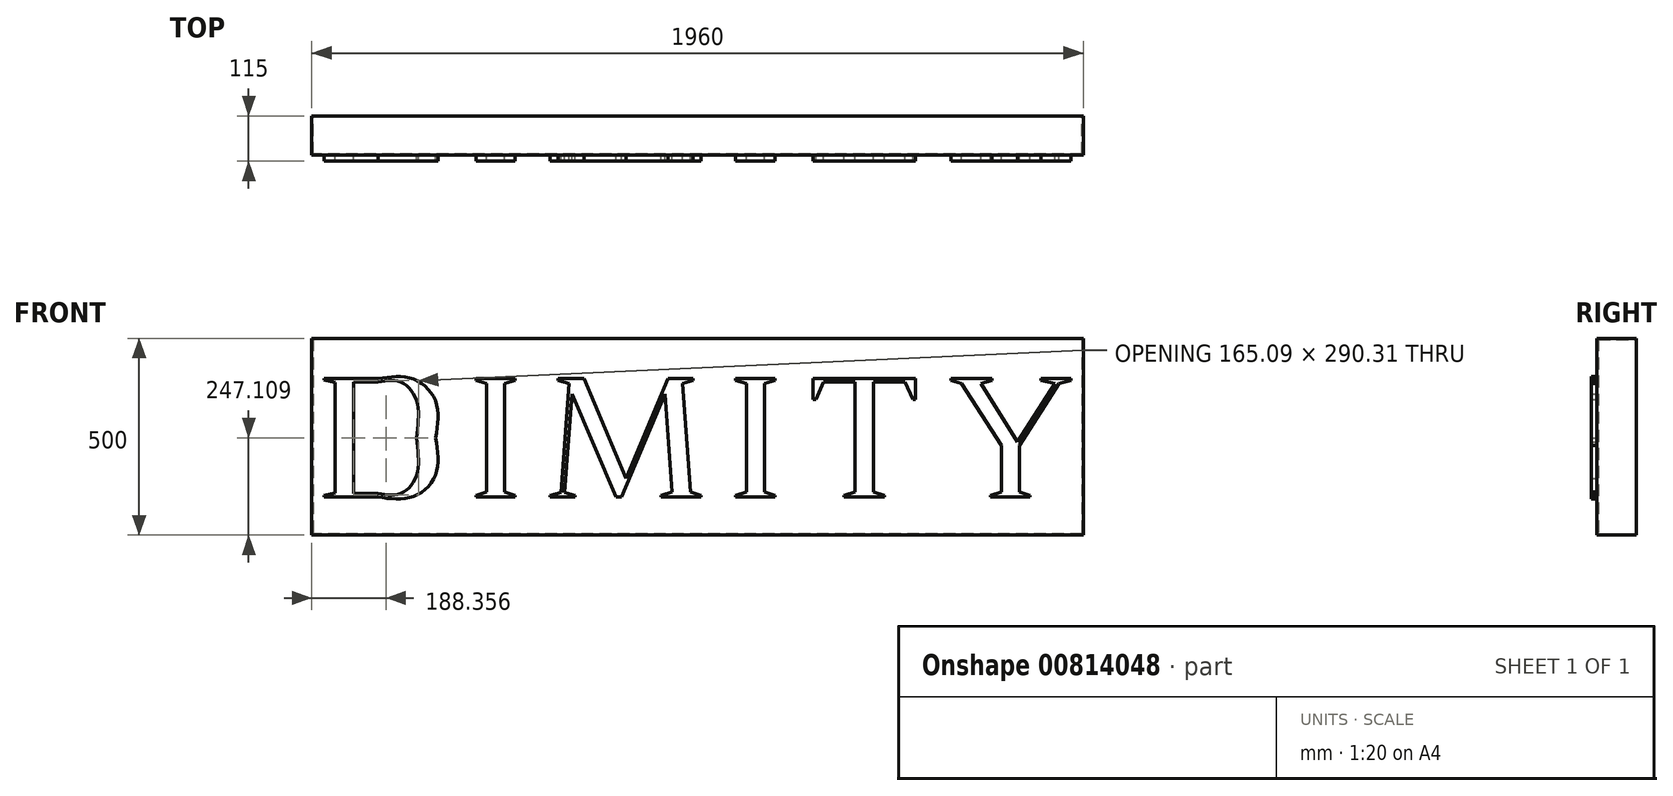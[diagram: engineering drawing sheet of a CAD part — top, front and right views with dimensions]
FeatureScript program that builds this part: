
annotation { "Feature Type Name" : "Feature", "Feature Type Description" : "" }
export const myFeature = defineFeature(function(context is Context, id is Id, definition is map)
    precondition{}
    {
        {
            var Q0;
            Q0=qCreatedBy(makeId("Front.planeOp"),FACE);
            var sketch = newSketch(context, id + "F0", { "sketchPlane" : qUnion([Q0])});
            skLineSegment(sketch, "E0", {"start": v(-948.48, 190.9) * mm, "end": v(-948.48, 187.03) * mm});
            skLineSegment(sketch, "E1", {"start": v(-948.48, 187.03) * mm, "end": v(-920.57, 180.59) * mm});
            skLineSegment(sketch, "E2", {"start": v(-920.57, 180.59) * mm, "end": v(-920.57, -99.41) * mm});
            skLineSegment(sketch, "E3", {"start": v(-920.57, -99.41) * mm, "end": v(-948.48, -106.29) * mm});
            skLineSegment(sketch, "E4", {"start": v(-948.48, -106.29) * mm, "end": v(-948.48, -109.72) * mm});
            skLineSegment(sketch, "E5", {"start": v(-948.48, -109.72) * mm, "end": v(-811.49, -109.72) * mm});
            skFitSpline(sketch, "E6", {"points": [v(-811.49, -109.72) * mm, v(-725.6, -109.72) * mm, v(-665.47, -53.9) * mm, v(-665.47, 40.59) * mm]});
            skFitSpline(sketch, "E7", {"points": [v(-665.47, 40.59) * mm, v(-665.47, 134.2) * mm, v(-725.6, 190.9) * mm, v(-811.49, 190.9) * mm]});
            skLineSegment(sketch, "E8", {"start": v(-811.49, 190.9) * mm, "end": v(-948.48, 190.9) * mm});
            skLineSegment(sketch, "E9", {"start": v(-874.19, 182.3) * mm, "end": v(-811.49, 182.3) * mm});
            skFitSpline(sketch, "E10", {"points": [v(-811.49, 182.3) * mm, v(-754.8, 182.3) * mm, v(-714, 135.07) * mm, v(-714, 40.16) * mm]});
            skFitSpline(sketch, "E11", {"points": [v(-714, 40.16) * mm, v(-714, -54.32) * mm, v(-754.8, -101.13) * mm, v(-811.49, -101.13) * mm]});
            skLineSegment(sketch, "E12", {"start": v(-811.49, -101.13) * mm, "end": v(-874.19, -101.13) * mm});
            skLineSegment(sketch, "E13", {"start": v(-874.19, -101.13) * mm, "end": v(-874.19, 182.3) * mm});
            skLineSegment(sketch, "E14", {"start": v(-563.25, 190.9) * mm, "end": v(-563.25, 186.6) * mm});
            skLineSegment(sketch, "E15", {"start": v(-563.25, 186.6) * mm, "end": v(-535.32, 178.44) * mm});
            skLineSegment(sketch, "E16", {"start": v(-535.32, 178.44) * mm, "end": v(-535.32, -97.27) * mm});
            skLineSegment(sketch, "E17", {"start": v(-535.32, -97.27) * mm, "end": v(-563.25, -105.43) * mm});
            skLineSegment(sketch, "E18", {"start": v(-563.25, -105.43) * mm, "end": v(-563.25, -109.72) * mm});
            skLineSegment(sketch, "E19", {"start": v(-563.25, -109.72) * mm, "end": v(-463.18, -109.72) * mm});
            skLineSegment(sketch, "E20", {"start": v(-463.18, -109.72) * mm, "end": v(-463.18, -105.43) * mm});
            skLineSegment(sketch, "E21", {"start": v(-463.18, -105.43) * mm, "end": v(-489.8, -97.27) * mm});
            skLineSegment(sketch, "E22", {"start": v(-489.8, -97.27) * mm, "end": v(-489.8, 178.44) * mm});
            skLineSegment(sketch, "E23", {"start": v(-489.8, 178.44) * mm, "end": v(-463.18, 186.6) * mm});
            skLineSegment(sketch, "E24", {"start": v(-463.18, 186.6) * mm, "end": v(-463.18, 190.9) * mm});
            skLineSegment(sketch, "E25", {"start": v(-463.18, 190.9) * mm, "end": v(-563.25, 190.9) * mm});
            skLineSegment(sketch, "E26", {"start": v(-354.1, 190.9) * mm, "end": v(-354.1, 186.6) * mm});
            skLineSegment(sketch, "E27", {"start": v(-354.1, 186.6) * mm, "end": v(-326.18, 178.44) * mm});
            skLineSegment(sketch, "E28", {"start": v(-326.18, 178.44) * mm, "end": v(-346.37, -98.13) * mm});
            skLineSegment(sketch, "E29", {"start": v(-346.37, -98.13) * mm, "end": v(-374.28, -106.29) * mm});
            skLineSegment(sketch, "E30", {"start": v(-374.28, -106.29) * mm, "end": v(-374.28, -109.72) * mm});
            skLineSegment(sketch, "E31", {"start": v(-374.28, -109.72) * mm, "end": v(-311.15, -109.72) * mm});
            skLineSegment(sketch, "E32", {"start": v(-311.15, -109.72) * mm, "end": v(-311.15, -106.29) * mm});
            skLineSegment(sketch, "E33", {"start": v(-311.15, -106.29) * mm, "end": v(-337.35, -98.13) * mm});
            skLineSegment(sketch, "E34", {"start": v(-337.35, -98.13) * mm, "end": v(-318.88, 151.82) * mm});
            skLineSegment(sketch, "E35", {"start": v(-318.88, 151.82) * mm, "end": v(-206.8, -109.72) * mm});
            skLineSegment(sketch, "E36", {"start": v(-206.8, -109.72) * mm, "end": v(-192.62, -109.72) * mm});
            skLineSegment(sketch, "E37", {"start": v(-192.62, -109.72) * mm, "end": v(-82.25, 151.39) * mm});
            skLineSegment(sketch, "E38", {"start": v(-82.25, 151.39) * mm, "end": v(-64.21, -97.27) * mm});
            skLineSegment(sketch, "E39", {"start": v(-64.21, -97.27) * mm, "end": v(-92.13, -105.43) * mm});
            skLineSegment(sketch, "E40", {"start": v(-92.13, -105.43) * mm, "end": v(-92.13, -109.72) * mm});
            skLineSegment(sketch, "E41", {"start": v(-92.13, -109.72) * mm, "end": v(8.36, -109.72) * mm});
            skLineSegment(sketch, "E42", {"start": v(8.36, -109.72) * mm, "end": v(8.36, -105.43) * mm});
            skLineSegment(sketch, "E43", {"start": v(8.36, -105.43) * mm, "end": v(-18.27, -97.27) * mm});
            skLineSegment(sketch, "E44", {"start": v(-18.27, -97.27) * mm, "end": v(-38.02, 178.44) * mm});
            skLineSegment(sketch, "E45", {"start": v(-38.02, 178.44) * mm, "end": v(-11.4, 186.6) * mm});
            skLineSegment(sketch, "E46", {"start": v(-11.4, 186.6) * mm, "end": v(-11.4, 190.9) * mm});
            skLineSegment(sketch, "E47", {"start": v(-11.4, 190.9) * mm, "end": v(-74.52, 190.9) * mm});
            skLineSegment(sketch, "E48", {"start": v(-74.52, 190.9) * mm, "end": v(-181.03, -62.48) * mm});
            skLineSegment(sketch, "E49", {"start": v(-181.03, -62.48) * mm, "end": v(-288.39, 190.9) * mm});
            skLineSegment(sketch, "E50", {"start": v(-288.39, 190.9) * mm, "end": v(-354.1, 190.9) * mm});
            skLineSegment(sketch, "E51", {"start": v(96.42, 190.9) * mm, "end": v(96.42, 186.6) * mm});
            skLineSegment(sketch, "E52", {"start": v(96.42, 186.6) * mm, "end": v(124.34, 178.44) * mm});
            skLineSegment(sketch, "E53", {"start": v(124.34, 178.44) * mm, "end": v(124.34, -97.27) * mm});
            skLineSegment(sketch, "E54", {"start": v(124.34, -97.27) * mm, "end": v(96.42, -105.43) * mm});
            skLineSegment(sketch, "E55", {"start": v(96.42, -105.43) * mm, "end": v(96.42, -109.72) * mm});
            skLineSegment(sketch, "E56", {"start": v(96.42, -109.72) * mm, "end": v(196.48, -109.72) * mm});
            skLineSegment(sketch, "E57", {"start": v(196.48, -109.72) * mm, "end": v(196.48, -105.43) * mm});
            skLineSegment(sketch, "E58", {"start": v(196.48, -105.43) * mm, "end": v(169.86, -97.27) * mm});
            skLineSegment(sketch, "E59", {"start": v(169.86, -97.27) * mm, "end": v(169.86, 178.44) * mm});
            skLineSegment(sketch, "E60", {"start": v(169.86, 178.44) * mm, "end": v(196.48, 186.6) * mm});
            skLineSegment(sketch, "E61", {"start": v(196.48, 186.6) * mm, "end": v(196.48, 190.9) * mm});
            skLineSegment(sketch, "E62", {"start": v(196.48, 190.9) * mm, "end": v(96.42, 190.9) * mm});
            skLineSegment(sketch, "E63", {"start": v(293.55, 190.9) * mm, "end": v(293.55, 138.07) * mm});
            skLineSegment(sketch, "E64", {"start": v(293.55, 138.07) * mm, "end": v(300.42, 138.07) * mm});
            skLineSegment(sketch, "E65", {"start": v(300.42, 138.07) * mm, "end": v(320.6, 182.3) * mm});
            skLineSegment(sketch, "E66", {"start": v(320.6, 182.3) * mm, "end": v(400.48, 182.3) * mm});
            skLineSegment(sketch, "E67", {"start": v(400.48, 182.3) * mm, "end": v(400.48, -97.27) * mm});
            skLineSegment(sketch, "E68", {"start": v(400.48, -97.27) * mm, "end": v(372.57, -105.43) * mm});
            skLineSegment(sketch, "E69", {"start": v(372.57, -105.43) * mm, "end": v(372.57, -109.72) * mm});
            skLineSegment(sketch, "E70", {"start": v(372.57, -109.72) * mm, "end": v(474.78, -109.72) * mm});
            skLineSegment(sketch, "E71", {"start": v(474.78, -109.72) * mm, "end": v(474.78, -105.43) * mm});
            skLineSegment(sketch, "E72", {"start": v(474.78, -105.43) * mm, "end": v(446.86, -97.27) * mm});
            skLineSegment(sketch, "E73", {"start": v(446.86, -97.27) * mm, "end": v(446.86, 182.3) * mm});
            skLineSegment(sketch, "E74", {"start": v(446.86, 182.3) * mm, "end": v(527.18, 182.3) * mm});
            skLineSegment(sketch, "E75", {"start": v(527.18, 182.3) * mm, "end": v(546.93, 138.07) * mm});
            skLineSegment(sketch, "E76", {"start": v(546.93, 138.07) * mm, "end": v(554.23, 138.07) * mm});
            skLineSegment(sketch, "E77", {"start": v(554.23, 138.07) * mm, "end": v(554.23, 190.9) * mm});
            skLineSegment(sketch, "E78", {"start": v(554.23, 190.9) * mm, "end": v(293.55, 190.9) * mm});
            skLineSegment(sketch, "E79", {"start": v(644.43, 190.9) * mm, "end": v(644.43, 186.6) * mm});
            skLineSegment(sketch, "E80", {"start": v(644.43, 186.6) * mm, "end": v(671.05, 178.44) * mm});
            skLineSegment(sketch, "E81", {"start": v(671.05, 178.44) * mm, "end": v(771.55, 20.83) * mm});
            skLineSegment(sketch, "E82", {"start": v(771.55, 20.83) * mm, "end": v(771.55, -97.27) * mm});
            skLineSegment(sketch, "E83", {"start": v(771.55, -97.27) * mm, "end": v(743.63, -105.43) * mm});
            skLineSegment(sketch, "E84", {"start": v(743.63, -105.43) * mm, "end": v(743.63, -109.72) * mm});
            skLineSegment(sketch, "E85", {"start": v(743.63, -109.72) * mm, "end": v(844.12, -109.72) * mm});
            skLineSegment(sketch, "E86", {"start": v(844.12, -109.72) * mm, "end": v(844.12, -105.43) * mm});
            skLineSegment(sketch, "E87", {"start": v(844.12, -105.43) * mm, "end": v(817.5, -97.27) * mm});
            skLineSegment(sketch, "E88", {"start": v(817.5, -97.27) * mm, "end": v(817.5, 20.83) * mm});
            skLineSegment(sketch, "E89", {"start": v(817.5, 20.83) * mm, "end": v(917.99, 178.44) * mm});
            skLineSegment(sketch, "E90", {"start": v(917.99, 178.44) * mm, "end": v(948.48, 186.6) * mm});
            skLineSegment(sketch, "E91", {"start": v(948.48, 186.6) * mm, "end": v(948.48, 190.9) * mm});
            skLineSegment(sketch, "E92", {"start": v(948.48, 190.9) * mm, "end": v(872.04, 190.9) * mm});
            skLineSegment(sketch, "E93", {"start": v(872.04, 190.9) * mm, "end": v(872.04, 186.6) * mm});
            skLineSegment(sketch, "E94", {"start": v(872.04, 186.6) * mm, "end": v(908.12, 178.44) * mm});
            skLineSegment(sketch, "E95", {"start": v(908.12, 178.44) * mm, "end": v(813.21, 30.28) * mm});
            skLineSegment(sketch, "E96", {"start": v(813.21, 30.28) * mm, "end": v(719.59, 178.44) * mm});
            skLineSegment(sketch, "E97", {"start": v(719.59, 178.44) * mm, "end": v(747.93, 186.6) * mm});
            skLineSegment(sketch, "E98", {"start": v(747.93, 186.6) * mm, "end": v(747.93, 190.9) * mm});
            skLineSegment(sketch, "E99", {"start": v(747.93, 190.9) * mm, "end": v(644.43, 190.9) * mm});
            skSolve(sketch);
        }
        {
            var Q0;
            Q0=qSketchRegion(id+"F0",true);
            extrude(context, id + "F1", {"entities" : qUnion([Q0]), "depth" : 15 * mm, "offsetDistance" : 25 * mm});
        }
        {
            var Q0;
            Q0=qCreatedBy(makeId("Front.planeOp"),FACE);
            var sketch = newSketch(context, id + "F2", { "sketchPlane" : qUnion([Q0])});
            skLineSegment(sketch, "E100.bottom", {"start": v(980, 293.5) * mm, "end": v(-980, 293.5) * mm});
            skLineSegment(sketch, "E100.top", {"start": v(980, -206.5) * mm, "end": v(-980, -206.5) * mm});
            skLineSegment(sketch, "E100.left", {"start": v(980, 293.5) * mm, "end": v(980, -206.5) * mm});
            skLineSegment(sketch, "E100.right", {"start": v(-980, 293.5) * mm, "end": v(-980, -206.5) * mm});
            skLineSegment(sketch, "E101", {"start": v(0, -206.5) * mm, "end": v(-980, -206.5) * mm, "construction": true});
            skLineSegment(sketch, "E102", {"start": v(-980, 268.5) * mm, "end": v(980, 268.5) * mm, "construction": true});
            skLineSegment(sketch, "E103", {"start": v(980, -181.5) * mm, "end": v(-980, -181.5) * mm, "construction": true});
            skLineSegment(sketch, "E104", {"start": v(-980, 43.5) * mm, "end": v(980, 43.5) * mm, "construction": true});
            skLineSegment(sketch, "E105", {"start": v(0, 293.5) * mm, "end": v(0, -206.5) * mm, "construction": true});
            skLineSegment(sketch, "E106", {"start": v(970, 293.5) * mm, "end": v(970, -206.5) * mm, "construction": true});
            skLineSegment(sketch, "E107", {"start": v(-970, 293.5) * mm, "end": v(-970, -206.5) * mm, "construction": true});
            skSolve(sketch);
        }
        {
            var Q0;
            Q0 = qSketchRegion(id + "F2", true);
            extrude(context, id + "F3", {"entities" : qUnion([Q0]), "oppositeDirection" : true, "depth" : 100 * mm, "offsetDistance" : 25 * mm});
        }
        {
            var Q0;
            Q0=makeQuery(id+"F3.opExtrude","CAP_FACE",FACE,{"disambiguationData":[OSD([sQuery(id+"F2.wireOp",EDGE,"E100.bottom"),sQuery(id+"F2.wireOp",EDGE,"E100.top"),sQuery(id+"F2.wireOp",EDGE,"E100.left"),sQuery(id+"F2.wireOp",EDGE,"E100.right")])],"isStart":false});
            var sketch = newSketch(context, id + "F4", { "sketchPlane" : qUnion([Q0])});
            skLineSegment(sketch, "E108", {"start": v(-977, 293.5) * mm, "end": v(-977, -206.5) * mm, "construction": true});
            skLineSegment(sketch, "E109", {"start": v(977, 293.5) * mm, "end": v(977, -206.5) * mm, "construction": true});
            skLineSegment(sketch, "E110", {"start": v(-980, -203.5) * mm, "end": v(980, -203.5) * mm, "construction": true});
            skLineSegment(sketch, "E111", {"start": v(-980, 290.5) * mm, "end": v(980, 290.5) * mm, "construction": true});
            skLineSegment(sketch, "E112.bottom", {"start": v(-977, 290.5) * mm, "end": v(977, 290.5) * mm});
            skLineSegment(sketch, "E112.top", {"start": v(-977, -203.5) * mm, "end": v(977, -203.5) * mm});
            skLineSegment(sketch, "E112.left", {"start": v(-977, 290.5) * mm, "end": v(-977, -203.5) * mm});
            skLineSegment(sketch, "E112.right", {"start": v(977, 290.5) * mm, "end": v(977, -203.5) * mm});
            skSolve(sketch);
        }
        {
            var Q0;
            Q0 = qSketchRegion(id + "F4", true);
            extrude(context, id + "F5", {"entities" : qUnion([Q0]), "operationType" : NewBodyOperationType.REMOVE, "oppositeDirection" : true, "depth" : 97 * mm, "offsetDistance" : 25 * mm});
        }
    });
